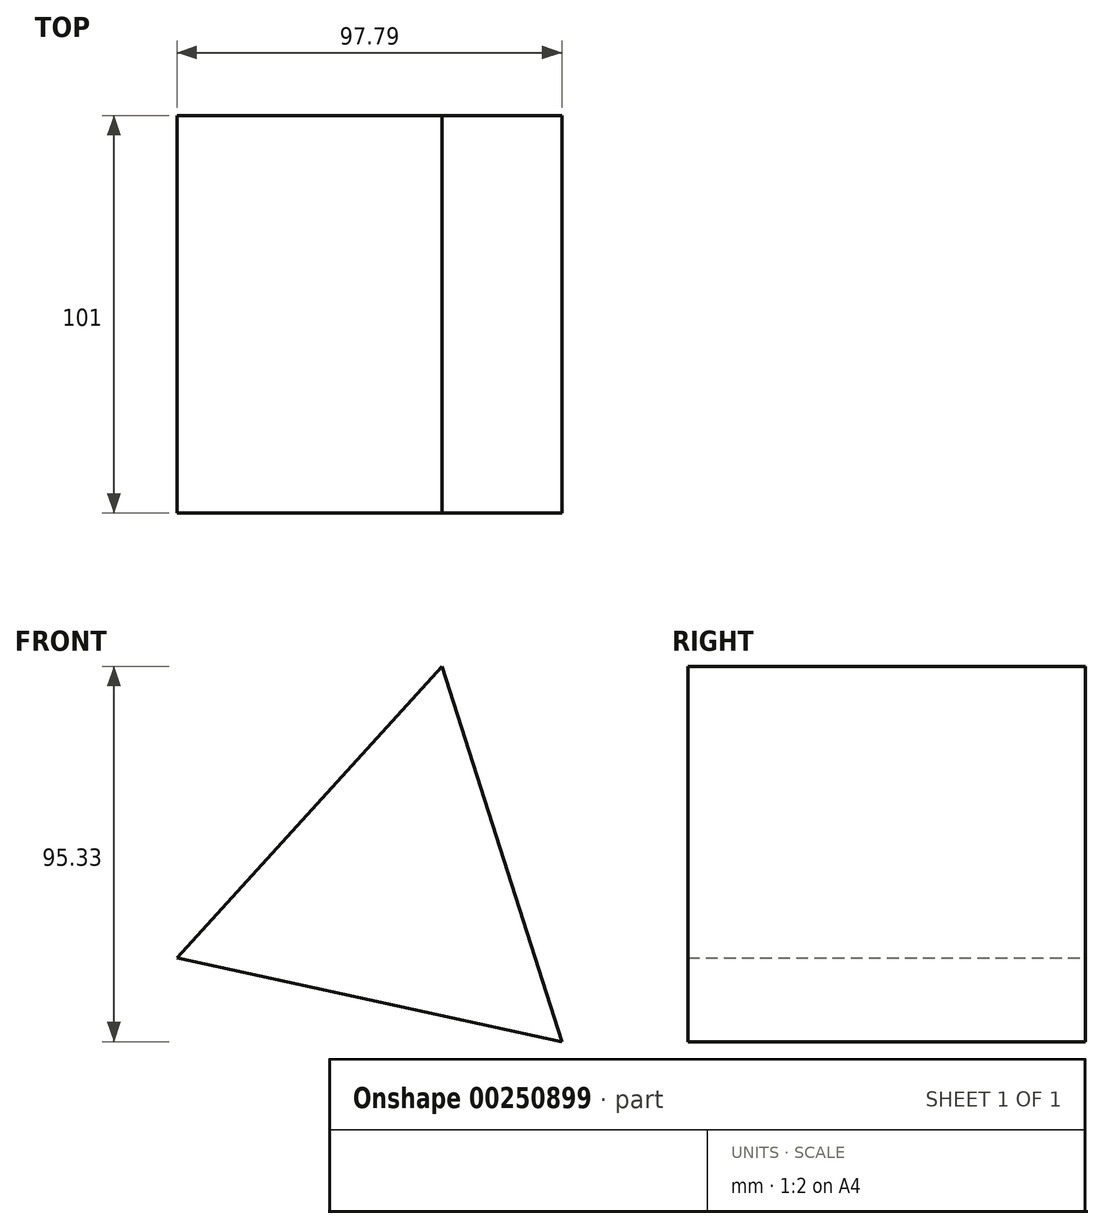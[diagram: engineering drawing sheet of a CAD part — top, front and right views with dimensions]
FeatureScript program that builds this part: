
annotation { "Feature Type Name" : "Feature", "Feature Type Description" : "" }
export const myFeature = defineFeature(function(context is Context, id is Id, definition is map)
    precondition{}
    {
        {
            var Q0;
            Q0=qCreatedBy(makeId("Front.planeOp"),FACE);
            var sketch = newSketch(context, id + "F0", { "sketchPlane" : qUnion([Q0])});
            skCircle(sketch, "E0.cCircle", {"center": v(0, 0) * mm, "radius": 57.78 * mm, "construction": true});
            skLineSegment(sketch, "E0.0", {"start": v(42.75, -38.87) * mm, "end": v(-55.04, -17.58) * mm});
            skLineSegment(sketch, "E0.1", {"start": v(-55.04, -17.58) * mm, "end": v(12.3, 56.46) * mm});
            skLineSegment(sketch, "E0.2", {"start": v(12.3, 56.46) * mm, "end": v(42.75, -38.87) * mm});
            skSolve(sketch);
        }
        {
            var Q0;
            Q0=makeQuery(id+"F0.imprint","IMPRINT",FACE,{"disambiguationData":[TD([[makeQuery(id+"F0.imprint","IMPRINT",EDGE,{"derivedFrom":sQuery(id+"F0.wireOp",EDGE,"E0.0")}),-1.0]])]});
            extrude(context, id + "F1", {"entities" : qUnion([Q0]), "endBound" : BoundingType.SYMMETRIC, "depth" : 101 * mm});
        }
    });
